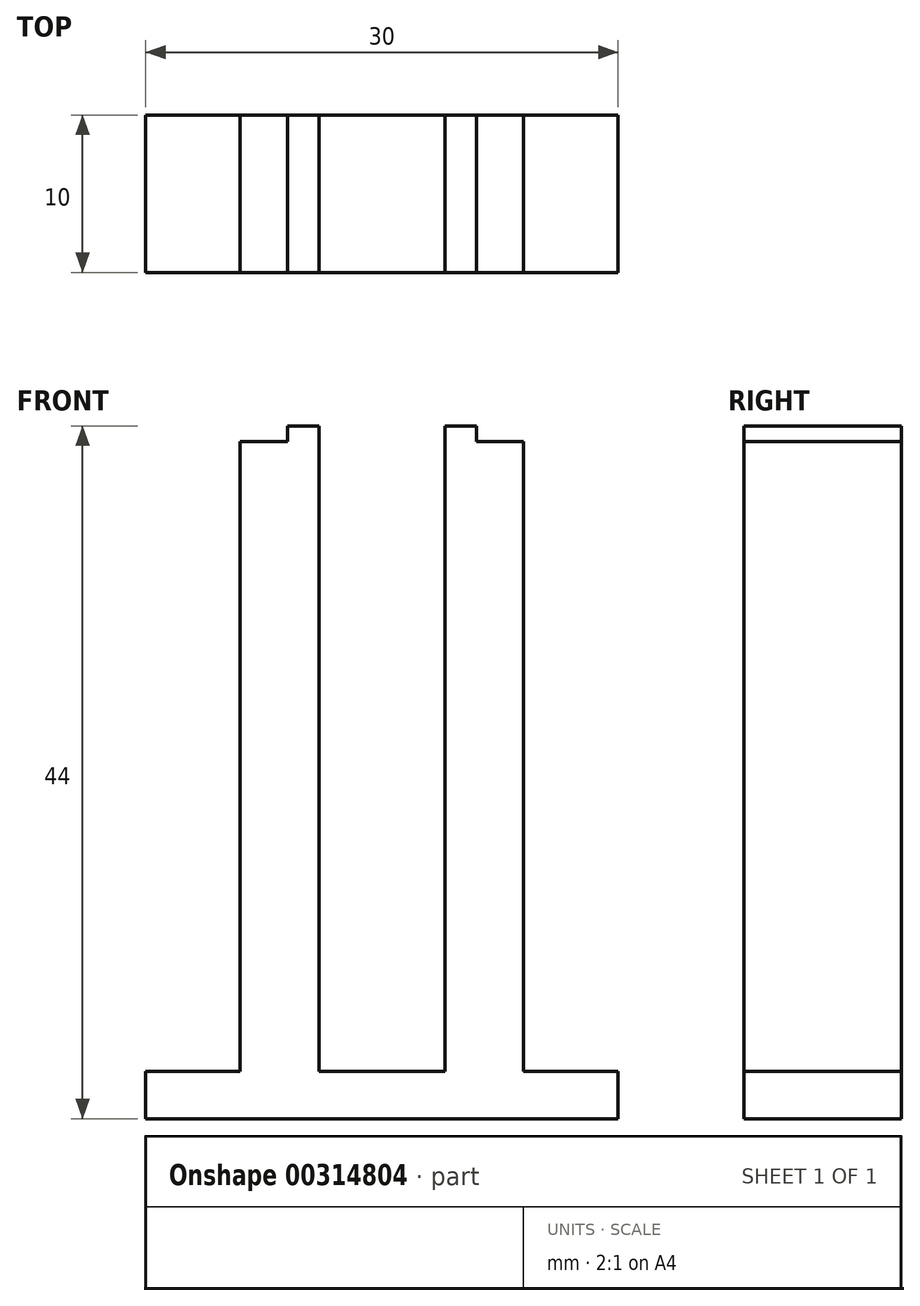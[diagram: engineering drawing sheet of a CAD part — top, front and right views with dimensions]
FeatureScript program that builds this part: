
annotation { "Feature Type Name" : "Feature", "Feature Type Description" : "" }
export const myFeature = defineFeature(function(context is Context, id is Id, definition is map)
    precondition{}
    {
        {
            var Q0;
            Q0=qCreatedBy(makeId("Top.planeOp"),FACE);
            var sketch = newSketch(context, id + "F0", { "sketchPlane" : qUnion([Q0])});
            skLineSegment(sketch, "E0.bottom", {"start": v(-15, -5) * mm, "end": v(15, -5) * mm});
            skLineSegment(sketch, "E0.top", {"start": v(-15, 5) * mm, "end": v(15, 5) * mm});
            skLineSegment(sketch, "E0.left", {"start": v(-15, -5) * mm, "end": v(-15, 5) * mm});
            skLineSegment(sketch, "E0.right", {"start": v(15, -5) * mm, "end": v(15, 5) * mm});
            skPoint(sketch, "E0.middle", {"position": v(0, 0) * mm});
            skLineSegment(sketch, "E1", {"start": v(-1, 5) * mm, "end": v(-1, -5) * mm, "construction": true});
            skLineSegment(sketch, "E2", {"start": v(1, 5) * mm, "end": v(1, -5) * mm, "construction": true});
            skLineSegment(sketch, "E3", {"start": v(-6, 5) * mm, "end": v(-6, -5) * mm});
            skLineSegment(sketch, "E4", {"start": v(6, 5) * mm, "end": v(6, -5) * mm});
            skLineSegment(sketch, "E5", {"start": v(9, 5) * mm, "end": v(9, -5) * mm});
            skLineSegment(sketch, "E6", {"start": v(-9, 5) * mm, "end": v(-9, -5) * mm});
            skLineSegment(sketch, "E7", {"start": v(4, -5) * mm, "end": v(4, 5) * mm});
            skLineSegment(sketch, "E8", {"start": v(-4, -5) * mm, "end": v(-4, 5) * mm});
            skSolve(sketch);
        }
        {
            var Q0;
            Q0 = qSketchRegion(id + "F0", true);
            var Q1;
            Q1 = qConstructionFilter(qBodyType(qCreatedBy(id + "F0" ,EDGE), BodyType.WIRE), ConstructionObject.NO);
            extrude(context, id + "F1", {"entities" : qUnion([Q0]), "surfaceEntities" : qUnion([Q1]), "depth" : 3 * mm, "offsetDistance" : 25 * mm});
        }
        {
            var Q0;
            {var subQ0=sQuery(id+"F0.wireOp",EDGE,"E4");Q0=makeQuery(id+"F0.imprint","IMPRINT",FACE,{"disambiguationData":[TD([[makeQuery(id+"F0.imprint","IMPRINT",EDGE,{"derivedFrom":subQ0}),1.0]])]});}
            var Q1;
            {var subQ0=sQuery(id+"F0.wireOp",EDGE,"E3");Q1=makeQuery(id+"F0.imprint","IMPRINT",FACE,{"disambiguationData":[TD([[makeQuery(id+"F0.imprint","IMPRINT",EDGE,{"derivedFrom":subQ0}),-1.0]])]});}
            extrude(context, id + "F2", {"entities" : qUnion([Q0, Q1]), "operationType" : NewBodyOperationType.ADD, "depth" : 43 * mm, "offsetDistance" : 25 * mm});
        }
        {
            var Q0;
            {var subQ0=sQuery(id+"F0.wireOp",EDGE,"E3");Q0=makeQuery(id+"F0.imprint","IMPRINT",FACE,{"disambiguationData":[TD([[makeQuery(id+"F0.imprint","IMPRINT",EDGE,{"derivedFrom":subQ0}),1.0]])]});}
            var Q1;
            {var subQ0=sQuery(id+"F0.wireOp",EDGE,"E4");Q1=makeQuery(id+"F0.imprint","IMPRINT",FACE,{"disambiguationData":[TD([[makeQuery(id+"F0.imprint","IMPRINT",EDGE,{"derivedFrom":subQ0}),-1.0]])]});}
            extrude(context, id + "F3", {"entities" : qUnion([Q0, Q1]), "operationType" : NewBodyOperationType.ADD, "depth" : 44 * mm, "offsetDistance" : 25 * mm});
        }
    });
